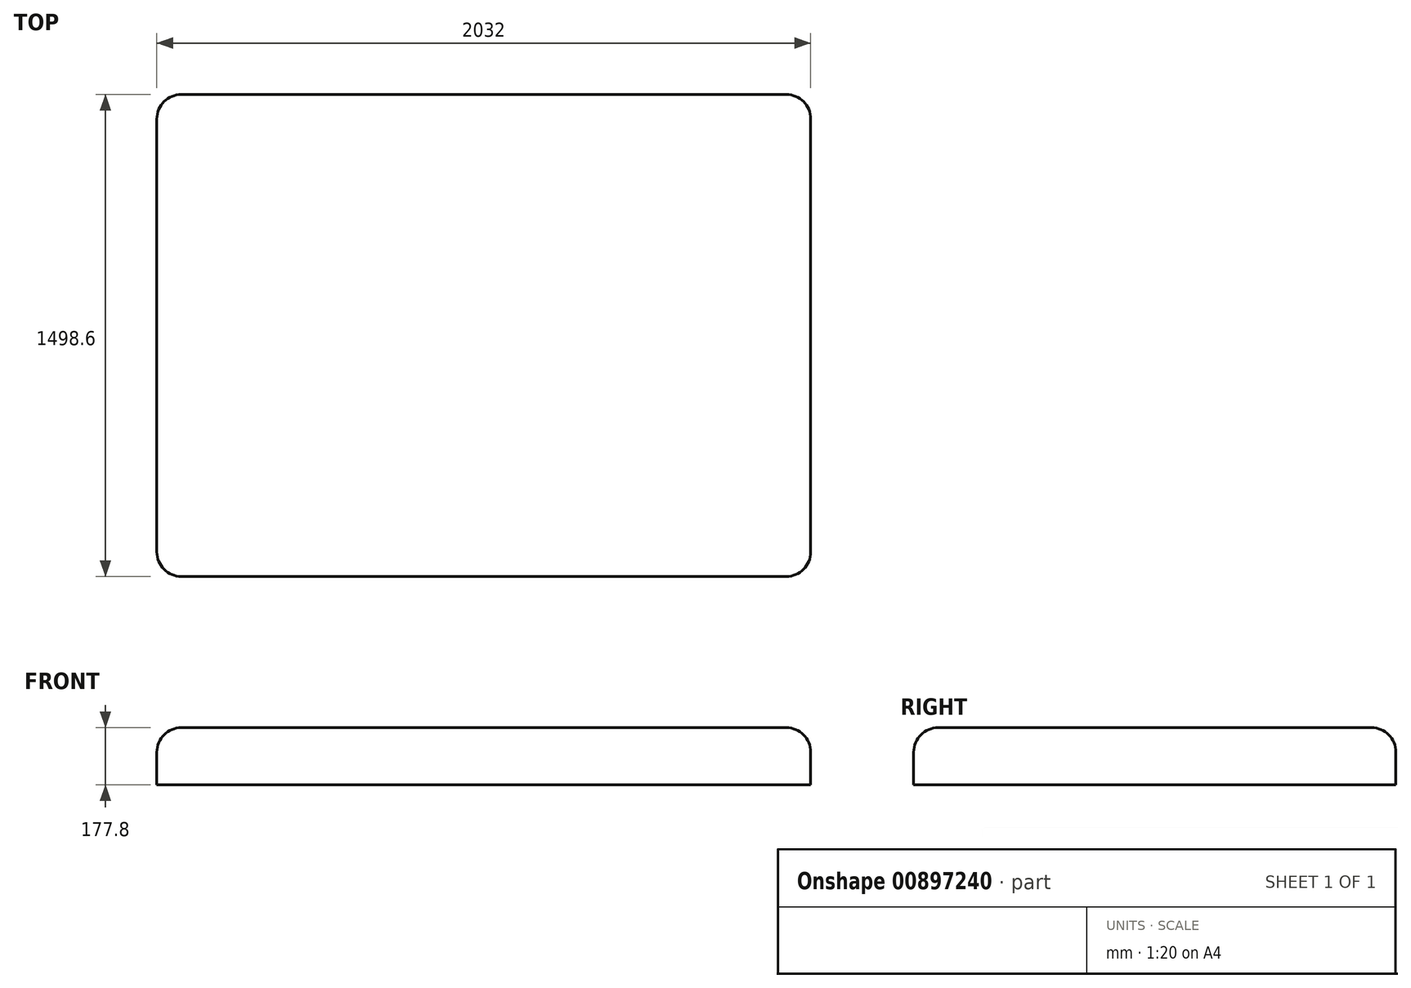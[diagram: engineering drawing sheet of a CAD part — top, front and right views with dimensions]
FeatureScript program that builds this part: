
annotation { "Feature Type Name" : "Feature", "Feature Type Description" : "" }
export const myFeature = defineFeature(function(context is Context, id is Id, definition is map)
    precondition{}
    {
        {
            var Q0;
            Q0=qCreatedBy(makeId("Top.planeOp"),FACE);
            var sketch = newSketch(context, id + "F0", { "sketchPlane" : qUnion([Q0])});
            skLineSegment(sketch, "E0.bottom", {"start": v(-1016, 749.3) * mm, "end": v(1016, 749.3) * mm});
            skLineSegment(sketch, "E0.top", {"start": v(-1016, -749.3) * mm, "end": v(1016, -749.3) * mm});
            skLineSegment(sketch, "E0.left", {"start": v(-1016, 749.3) * mm, "end": v(-1016, -749.3) * mm});
            skLineSegment(sketch, "E0.right", {"start": v(1016, 749.3) * mm, "end": v(1016, -749.3) * mm});
            skPoint(sketch, "E0.middle", {"position": v(0, 0) * mm});
            skSolve(sketch);
        }
        {
            var Q0;
            Q0=makeQuery(id+"F0.imprint","IMPRINT",FACE,{"disambiguationData":[TD([[makeQuery(id+"F0.imprint","IMPRINT",EDGE,{"derivedFrom":sQuery(id+"F0.wireOp",EDGE,"E0.bottom")}),-1.0]])]});
            extrude(context, id + "F1", {"entities" : qUnion([Q0]), "depth" : 177.8 * mm, "offsetDistance" : 25.4 * mm});
        }
        {
            var Q0;
            Q0=makeQuery(id+"F1.opExtrude","SWEPT_EDGE",EDGE,{"disambiguationData":[OSD([sQuery(id+"F0.wireOp",EDGE,"E0.top"),sQuery(id+"F0.wireOp",EDGE,"E0.left")])]});
            var Q1;
            Q1=makeQuery(id+"F1.opExtrude","SWEPT_EDGE",EDGE,{"disambiguationData":[OSD([sQuery(id+"F0.wireOp",EDGE,"E0.top"),sQuery(id+"F0.wireOp",EDGE,"E0.right")])]});
            var Q2;
            Q2=makeQuery(id+"F1.opExtrude","SWEPT_EDGE",EDGE,{"disambiguationData":[OSD([sQuery(id+"F0.wireOp",EDGE,"E0.bottom"),sQuery(id+"F0.wireOp",EDGE,"E0.right")])]});
            var Q3;
            Q3=makeQuery(id+"F1.opExtrude","SWEPT_EDGE",EDGE,{"disambiguationData":[OSD([sQuery(id+"F0.wireOp",EDGE,"E0.bottom"),sQuery(id+"F0.wireOp",EDGE,"E0.left")])]});
            var Q4;
            Q4=makeQuery(id+"F1.opExtrude","CAP_EDGE",EDGE,{"disambiguationData":[OSD([sQuery(id+"F0.wireOp",EDGE,"E0.left")])],"isStart":false});
            var Q5;
            Q5=makeQuery(id+"F1.opExtrude","CAP_EDGE",EDGE,{"disambiguationData":[OSD([sQuery(id+"F0.wireOp",EDGE,"E0.bottom")])],"isStart":false});
            var Q6;
            Q6=makeQuery(id+"F1.opExtrude","CAP_EDGE",EDGE,{"disambiguationData":[OSD([sQuery(id+"F0.wireOp",EDGE,"E0.top")])],"isStart":false});
            var Q7;
            Q7=makeQuery(id+"F1.opExtrude","CAP_EDGE",EDGE,{"disambiguationData":[OSD([sQuery(id+"F0.wireOp",EDGE,"E0.right")])],"isStart":false});
            fillet(context, id + "F2", {"entities" : qUnion([Q0, Q1, Q2, Q3, Q4, Q5, Q6, Q7]), "radius" : 76.2 * mm, "tangentPropagation" : true, "allowEdgeOverflow" : false});
        }
    });
